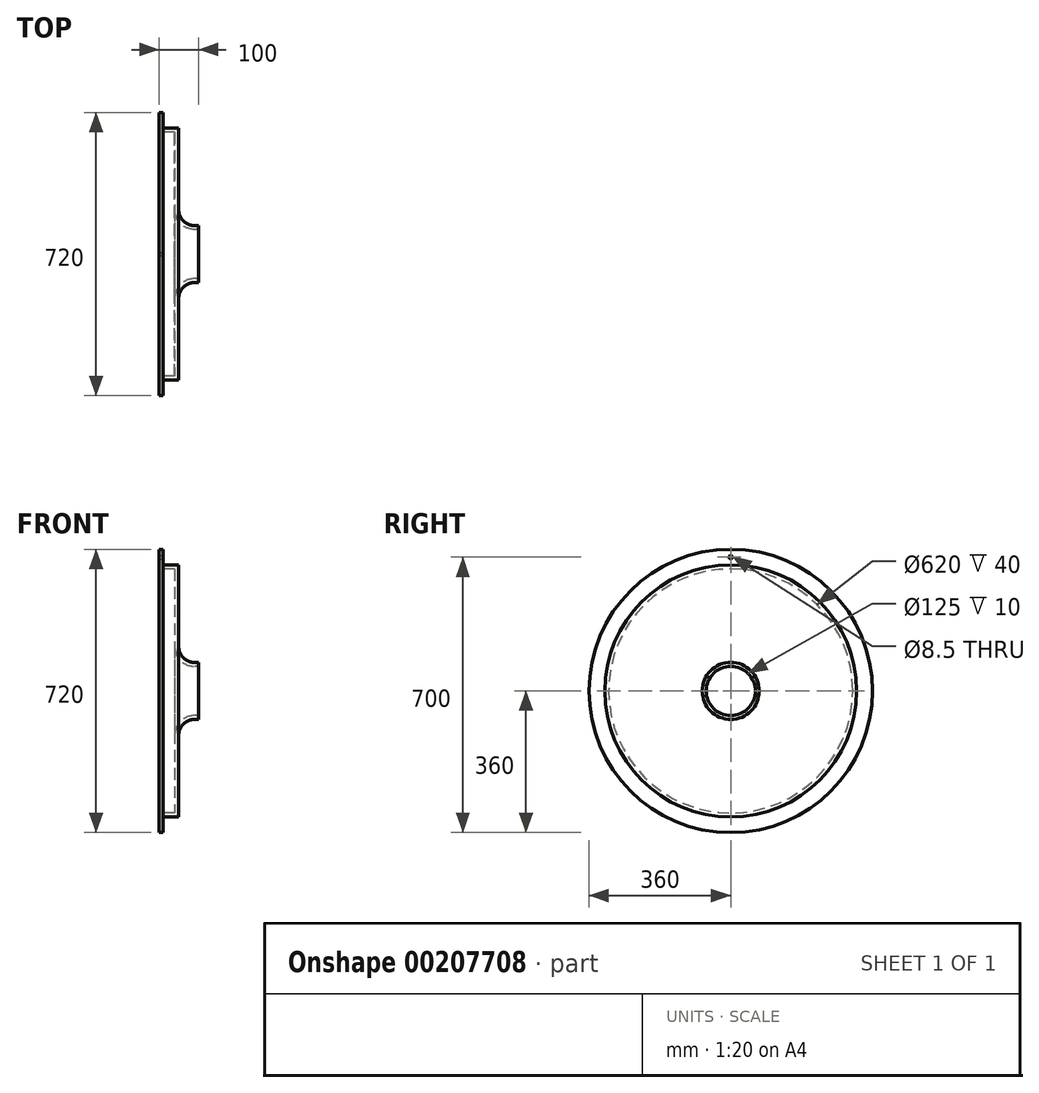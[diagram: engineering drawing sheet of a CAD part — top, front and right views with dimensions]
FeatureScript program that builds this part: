
annotation { "Feature Type Name" : "Feature", "Feature Type Description" : "" }
export const myFeature = defineFeature(function(context is Context, id is Id, definition is map)
    precondition{}
    {
        {
            var Q0;
            Q0=qCreatedBy(makeId("Front.planeOp"),FACE);
            var sketch = newSketch(context, id + "F0", { "sketchPlane" : qUnion([Q0])});
            skArc(sketch, "E0", {"start": v(40, 112.5) * mm, "mid": v(54.64, 77.14) * mm, "end": v(90, 62.5) * mm});
            skLineSegment(sketch, "E1", {"start": v(90, 62.5) * mm, "end": v(100, 62.5) * mm});
            skLineSegment(sketch, "E2", {"start": v(0, 310) * mm, "end": v(40, 310) * mm});
            skLineSegment(sketch, "E3", {"start": v(40, 310) * mm, "end": v(40, 112.5) * mm});
            skLineSegment(sketch, "E4", {"start": v(0, 360) * mm, "end": v(0, 310) * mm});
            skLineSegment(sketch, "E5.0", {"start": v(90, 72.5) * mm, "end": v(100, 72.5) * mm});
            skLineSegment(sketch, "E5.1", {"start": v(10, 360) * mm, "end": v(10, 320) * mm});
            skLineSegment(sketch, "E5.2", {"start": v(10, 320) * mm, "end": v(50, 320) * mm});
            skLineSegment(sketch, "E5.3", {"start": v(50, 320) * mm, "end": v(50, 112.5) * mm});
            skArc(sketch, "E5.4", {"start": v(50, 112.5) * mm, "mid": v(61.72, 84.22) * mm, "end": v(90, 72.5) * mm});
            skLineSegment(sketch, "E6", {"start": v(0, 360) * mm, "end": v(10, 360) * mm});
            skLineSegment(sketch, "E7", {"start": v(100, 72.5) * mm, "end": v(100, 62.5) * mm});
            skLineSegment(sketch, "E8", {"start": v(0, 0) * mm, "end": v(100, 0) * mm, "construction": true});
            skSolve(sketch);
        }
        {
            var Q0;
            Q0 = qSketchRegion(id + "F0", true);
            var Q1;
            Q1=sQuery(id+"F0.wireOp",EDGE,"E8");
            revolve(context, id + "F1", {"entities" : qUnion([Q0]), "axis" : qUnion([Q1]), "revolveType" : RevolveType.FULL});
        }
        {
            var Q0;
            Q0=makeQuery(id+"F1.opRevolve","SWEPT_FACE",FACE,{"disambiguationData":[OSD([sQuery(id+"F0.wireOp",EDGE,"E5.1")])]});
            var sketch = newSketch(context, id + "F2", { "sketchPlane" : qUnion([Q0])});
            skCircle(sketch, "E9", {"center": v(0, 340) * mm, "radius": 5 * mm});
            skSolve(sketch);
        }
        {
            var Q0;
            Q0=sQuery(id+"F2.wireOp",VERTEX,"E9.center");
            var Q1;
            Q1=makeQuery(id+"F1.opRevolve","SWEPT_BODY",BODY,{"disambiguationData":[OSD([sQuery(id+"F0.wireOp",EDGE,"E0"),sQuery(id+"F0.wireOp",EDGE,"E1"),sQuery(id+"F0.wireOp",EDGE,"E2"),sQuery(id+"F0.wireOp",EDGE,"E3"),sQuery(id+"F0.wireOp",EDGE,"E4"),sQuery(id+"F0.wireOp",EDGE,"E5.0"),sQuery(id+"F0.wireOp",EDGE,"E5.1"),sQuery(id+"F0.wireOp",EDGE,"E5.2"),sQuery(id+"F0.wireOp",EDGE,"E5.3"),sQuery(id+"F0.wireOp",EDGE,"E5.4"),sQuery(id+"F0.wireOp",EDGE,"E6"),sQuery(id+"F0.wireOp",EDGE,"E7")])]});
            hole(context, id + "F3", {"style" : HoleStyle.SIMPLE, "endStyle" : HoleEndStyle.THROUGH, "standardTappedOrClearance" : lookupTablePath({ "standard" : "ISO", "engagement" : "75%", "pitch" : "1.5 mm", "size" : "M10", "type" : "Tapped" }), "standardBlindInLast" : lookupTablePath({ "standard" : "ISO", "engagement" : "75%", "pitch" : "1.5 mm", "size" : "M10", "type" : "Tapped" }), "holeDiameter" : 8.5 * mm, "showTappedDepth" : true, "tappedDepth" : 12 * mm, "tapClearance" : 3, "locations" : qUnion([Q0]), "scope" : qUnion([Q1]), "majorDiameter" : 10 * mm});
        }
    });
